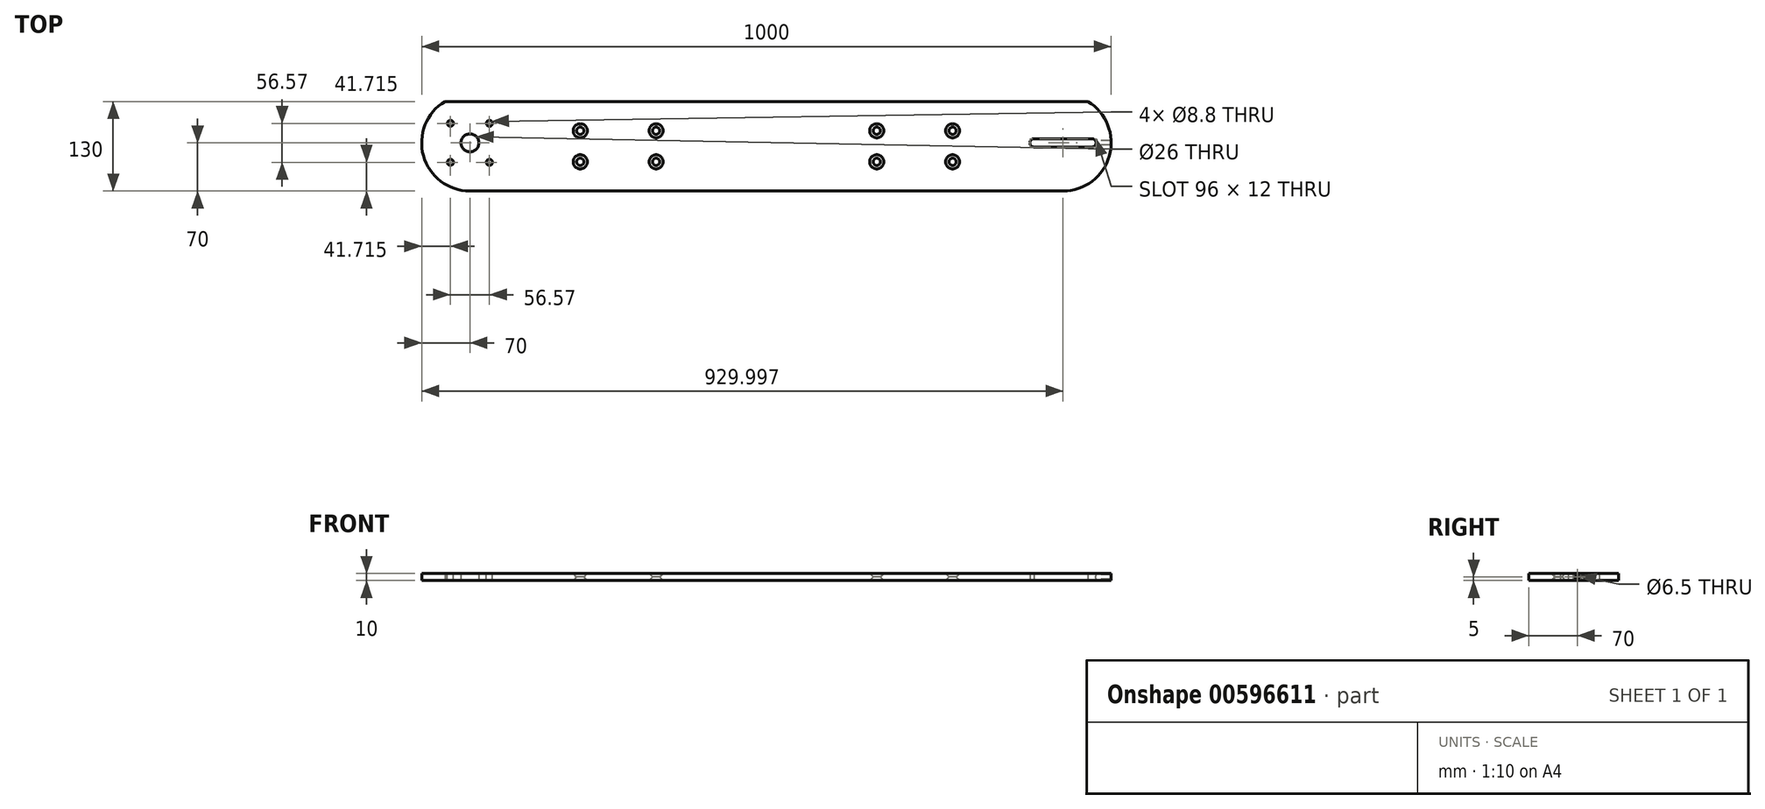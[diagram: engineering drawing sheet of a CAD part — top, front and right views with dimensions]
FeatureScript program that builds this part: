
annotation { "Feature Type Name" : "Feature", "Feature Type Description" : "" }
export const myFeature = defineFeature(function(context is Context, id is Id, definition is map)
    precondition{}
    {
        {
            var Q0;
            Q0=qCreatedBy(makeId("Top.planeOp"),FACE);
            var sketch = newSketch(context, id + "F0", { "sketchPlane" : qUnion([Q0])});
            skLineSegment(sketch, "E0", {"start": v(-466.06, 65) * mm, "end": v(466.06, 65) * mm});
            skLineSegment(sketch, "E1", {"start": v(472.27, -1) * mm, "end": v(387.99, -1) * mm});
            skLineSegment(sketch, "E2", {"start": v(472.27, 11) * mm, "end": v(388.13, 11) * mm});
            skArc(sketch, "E3", {"start": v(430, -65) * mm, "mid": v(497.45, -13.7) * mm, "end": v(466.06, 65) * mm});
            skLineSegment(sketch, "E4", {"start": v(430, -65) * mm, "end": v(-430, -65) * mm});
            skArc(sketch, "E5", {"start": v(-466.06, 65) * mm, "mid": v(-497.45, -13.7) * mm, "end": v(-430, -65) * mm});
            skCircle(sketch, "E6", {"center": v(-430, 5) * mm, "radius": 13 * mm});
            skCircle(sketch, "E7", {"center": v(-160, -22.5) * mm, "radius": 5.25 * mm});
            skCircle(sketch, "E8", {"center": v(-160, 22.5) * mm, "radius": 5.25 * mm});
            skCircle(sketch, "E9", {"center": v(-270, -22.5) * mm, "radius": 5.25 * mm});
            skCircle(sketch, "E10", {"center": v(-270, 22.5) * mm, "radius": 5.25 * mm});
            skCircle(sketch, "E11", {"center": v(160, -22.5) * mm, "radius": 5.25 * mm});
            skCircle(sketch, "E12", {"center": v(160, 22.5) * mm, "radius": 5.25 * mm});
            skCircle(sketch, "E13", {"center": v(270, -22.5) * mm, "radius": 5.25 * mm});
            skCircle(sketch, "E14", {"center": v(270, 22.5) * mm, "radius": 5.25 * mm});
            skArc(sketch, "E15", {"start": v(472, -1) * mm, "mid": v(478, 5) * mm, "end": v(472, 11) * mm});
            skArc(sketch, "E16", {"start": v(388.13, 11) * mm, "mid": v(382, 5.07) * mm, "end": v(387.99, -1) * mm});
            skCircle(sketch, "E17", {"center": v(-458.29, 33.28) * mm, "radius": 3.4 * mm});
            skCircle(sketch, "E18", {"center": v(-401.72, 33.28) * mm, "radius": 3.4 * mm});
            skCircle(sketch, "E19", {"center": v(-401.72, -23.29) * mm, "radius": 3.4 * mm});
            skCircle(sketch, "E20", {"center": v(-458.29, -23.29) * mm, "radius": 3.4 * mm});
            skSolve(sketch);
        }
        {
            var Q0;
            Q0 = qSketchRegion(id + "F0", true);
            extrude(context, id + "F1", {"entities" : qUnion([Q0]), "depth" : 10 * mm, "offsetDistance" : 25 * mm});
        }
        {
            var Q0;
            Q0=makeQuery(id+"F1.opExtrude","CAP_FACE",FACE,{"disambiguationData":[OSD([sQuery(id+"F0.wireOp",EDGE,"E0"),sQuery(id+"F0.wireOp",EDGE,"E1"),sQuery(id+"F0.wireOp",EDGE,"E2"),sQuery(id+"F0.wireOp",EDGE,"E3"),sQuery(id+"F0.wireOp",EDGE,"E4"),sQuery(id+"F0.wireOp",EDGE,"E5"),sQuery(id+"F0.wireOp",EDGE,"E6"),sQuery(id+"F0.wireOp",EDGE,"E7"),sQuery(id+"F0.wireOp",EDGE,"E8"),sQuery(id+"F0.wireOp",EDGE,"E9"),sQuery(id+"F0.wireOp",EDGE,"E10"),sQuery(id+"F0.wireOp",EDGE,"E11"),sQuery(id+"F0.wireOp",EDGE,"E12"),sQuery(id+"F0.wireOp",EDGE,"E13"),sQuery(id+"F0.wireOp",EDGE,"E14"),sQuery(id+"F0.wireOp",EDGE,"E15"),sQuery(id+"F0.wireOp",EDGE,"E16"),sQuery(id+"F0.wireOp",EDGE,"E17"),sQuery(id+"F0.wireOp",EDGE,"E18"),sQuery(id+"F0.wireOp",EDGE,"E19"),sQuery(id+"F0.wireOp",EDGE,"E20")])],"isStart":false});
            var sketch = newSketch(context, id + "F2", { "sketchPlane" : qUnion([Q0])});
            skPoint(sketch, "E21", {"position": v(-458.29, 33.28) * mm});
            skPoint(sketch, "E22", {"position": v(-401.72, 33.28) * mm});
            skPoint(sketch, "E23", {"position": v(-401.72, -23.29) * mm});
            skPoint(sketch, "E24", {"position": v(-458.29, -23.29) * mm});
            skSolve(sketch);
        }
        {
            var Q0;
            Q0=sQuery(id+"F2.wireOp",VERTEX,"E24");
            var Q1;
            Q1=sQuery(id+"F2.wireOp",VERTEX,"E23");
            var Q2;
            Q2=sQuery(id+"F2.wireOp",VERTEX,"E22");
            var Q3;
            Q3=sQuery(id+"F2.wireOp",VERTEX,"E21");
            var Q4;
            Q4=makeQuery(id+"F1.opExtrude","SWEPT_BODY",BODY,{"disambiguationData":[OSD([sQuery(id+"F0.wireOp",EDGE,"E0"),sQuery(id+"F0.wireOp",EDGE,"E1"),sQuery(id+"F0.wireOp",EDGE,"E2"),sQuery(id+"F0.wireOp",EDGE,"E3"),sQuery(id+"F0.wireOp",EDGE,"E4"),sQuery(id+"F0.wireOp",EDGE,"E5"),sQuery(id+"F0.wireOp",EDGE,"E6"),sQuery(id+"F0.wireOp",EDGE,"E7"),sQuery(id+"F0.wireOp",EDGE,"E8"),sQuery(id+"F0.wireOp",EDGE,"E9"),sQuery(id+"F0.wireOp",EDGE,"E10"),sQuery(id+"F0.wireOp",EDGE,"E11"),sQuery(id+"F0.wireOp",EDGE,"E12"),sQuery(id+"F0.wireOp",EDGE,"E13"),sQuery(id+"F0.wireOp",EDGE,"E14"),sQuery(id+"F0.wireOp",EDGE,"E15"),sQuery(id+"F0.wireOp",EDGE,"E16"),sQuery(id+"F0.wireOp",EDGE,"E17"),sQuery(id+"F0.wireOp",EDGE,"E18"),sQuery(id+"F0.wireOp",EDGE,"E19"),sQuery(id+"F0.wireOp",EDGE,"E20")])]});
            hole(context, id + "F3", {"style" : HoleStyle.SIMPLE, "endStyle" : HoleEndStyle.THROUGH, "standardTappedOrClearance" : lookupTablePath({ "standard" : "ISO", "fit" : "Normal", "size" : "M8", "type" : "Clearance" }), "standardBlindInLast" : lookupTablePath({ "standard" : "ISO", "fit" : "Standard", "size" : "M8", "type" : "Clearance" }), "holeDiameter" : 8.8 * mm, "majorDiameter" : 5 * mm, "isTappedThrough" : true, "tappedDepth" : 12 * mm, "tapClearance" : 3, "startFromSketch" : true, "locations" : qUnion([Q0, Q1, Q2, Q3]), "scope" : qUnion([Q4])});
        }
        {
            var Q0;
            Q0=qCreatedBy(makeId("Right.planeOp"),FACE);
            cPlane(context, id + "F4", {"entities" : qUnion([Q0]), "cplaneType" : CPlaneType.OFFSET, "offset" : 457 * mm, "width" : 150 * mm, "height" : 150 * mm});
        }
        {
            var Q0;
            Q0=qCreatedBy(id+"F4.planeOp",FACE);
            var sketch = newSketch(context, id + "F5", { "sketchPlane" : qUnion([Q0])});
            skCircle(sketch, "E25", {"center": v(5, 5) * mm, "radius": 3.25 * mm});
            skSolve(sketch);
        }
        {
            var Q0;
            Q0 = qSketchRegion(id + "F5", true);
            extrude(context, id + "F6", {"entities" : qUnion([Q0]), "operationType" : NewBodyOperationType.REMOVE, "endBound" : BoundingType.THROUGH_ALL, "depth" : 25 * mm, "offsetDistance" : 25 * mm});
        }
        {
            var Q0;
            Q0=makeQuery(id+"F1.opExtrude","CAP_EDGE",EDGE,{"disambiguationData":[OSD([sQuery(id+"F0.wireOp",EDGE,"E9")])],"isStart":false});
            var Q1;
            Q1=makeQuery(id+"F1.opExtrude","CAP_EDGE",EDGE,{"disambiguationData":[OSD([sQuery(id+"F0.wireOp",EDGE,"E10")])],"isStart":false});
            var Q2;
            Q2=makeQuery(id+"F1.opExtrude","CAP_EDGE",EDGE,{"disambiguationData":[OSD([sQuery(id+"F0.wireOp",EDGE,"E7")])],"isStart":false});
            var Q3;
            Q3=makeQuery(id+"F1.opExtrude","CAP_EDGE",EDGE,{"disambiguationData":[OSD([sQuery(id+"F0.wireOp",EDGE,"E8")])],"isStart":false});
            chamfer(context, id + "F7", {"entities" : qUnion([Q0, Q1, Q2, Q3]), "width" : 5 * mm, "tangentPropagation" : true});
        }
        {
            var Q0;
            Q0=makeQuery(id+"F1.opExtrude","CAP_EDGE",EDGE,{"disambiguationData":[OSD([sQuery(id+"F0.wireOp",EDGE,"E14")])],"isStart":false});
            var Q1;
            Q1=makeQuery(id+"F1.opExtrude","CAP_EDGE",EDGE,{"disambiguationData":[OSD([sQuery(id+"F0.wireOp",EDGE,"E13")])],"isStart":false});
            var Q2;
            Q2=makeQuery(id+"F1.opExtrude","CAP_EDGE",EDGE,{"disambiguationData":[OSD([sQuery(id+"F0.wireOp",EDGE,"E11")])],"isStart":false});
            var Q3;
            Q3=makeQuery(id+"F1.opExtrude","CAP_EDGE",EDGE,{"disambiguationData":[OSD([sQuery(id+"F0.wireOp",EDGE,"E12")])],"isStart":false});
            chamfer(context, id + "F8", {"entities" : qUnion([Q0, Q1, Q2, Q3]), "width" : 5 * mm, "tangentPropagation" : true});
        }
        {
            var Q0;
            Q0=makeQuery(id+"F1.opExtrude","CAP_EDGE",EDGE,{"disambiguationData":[OSD([sQuery(id+"F0.wireOp",EDGE,"E13")])],"isStart":true});
            var Q1;
            Q1=makeQuery(id+"F1.opExtrude","CAP_EDGE",EDGE,{"disambiguationData":[OSD([sQuery(id+"F0.wireOp",EDGE,"E14")])],"isStart":true});
            var Q2;
            Q2=makeQuery(id+"F1.opExtrude","CAP_EDGE",EDGE,{"disambiguationData":[OSD([sQuery(id+"F0.wireOp",EDGE,"E12")])],"isStart":true});
            var Q3;
            Q3=makeQuery(id+"F1.opExtrude","CAP_EDGE",EDGE,{"disambiguationData":[OSD([sQuery(id+"F0.wireOp",EDGE,"E11")])],"isStart":true});
            var Q4;
            Q4=makeQuery(id+"F1.opExtrude","CAP_EDGE",EDGE,{"disambiguationData":[OSD([sQuery(id+"F0.wireOp",EDGE,"E8")])],"isStart":true});
            var Q5;
            Q5=makeQuery(id+"F1.opExtrude","CAP_EDGE",EDGE,{"disambiguationData":[OSD([sQuery(id+"F0.wireOp",EDGE,"E7")])],"isStart":true});
            var Q6;
            Q6=makeQuery(id+"F1.opExtrude","CAP_EDGE",EDGE,{"disambiguationData":[OSD([sQuery(id+"F0.wireOp",EDGE,"E10")])],"isStart":true});
            var Q7;
            Q7=makeQuery(id+"F1.opExtrude","CAP_EDGE",EDGE,{"disambiguationData":[OSD([sQuery(id+"F0.wireOp",EDGE,"E9")])],"isStart":true});
            chamfer(context, id + "F9", {"entities" : qUnion([Q0, Q1, Q2, Q3, Q4, Q5, Q6, Q7]), "width" : 5 * mm, "tangentPropagation" : true});
        }
    });
